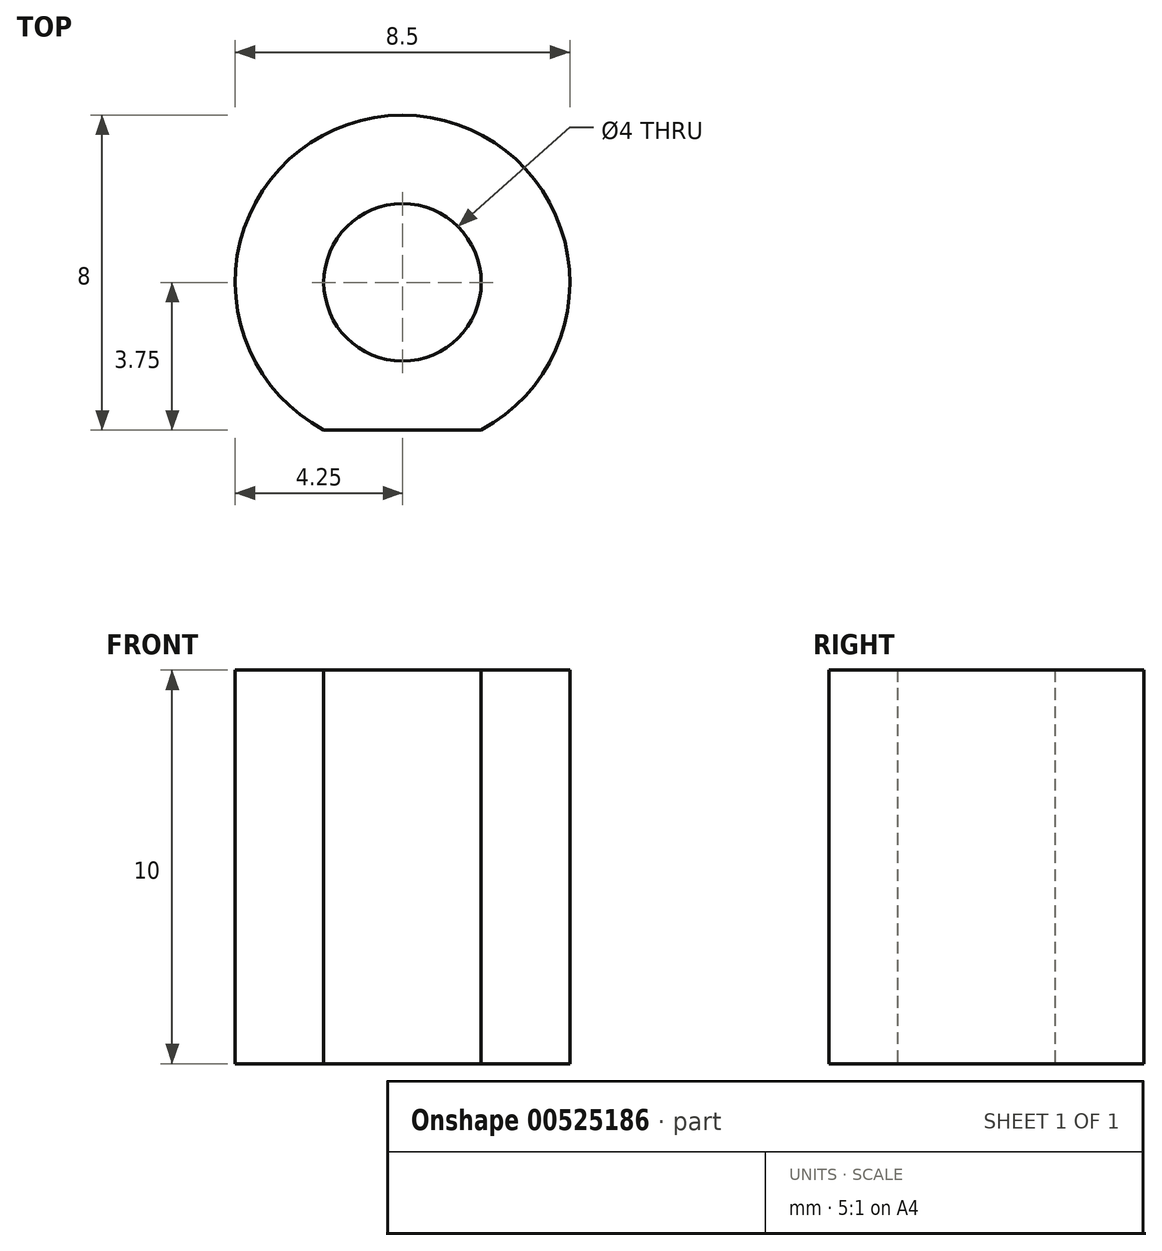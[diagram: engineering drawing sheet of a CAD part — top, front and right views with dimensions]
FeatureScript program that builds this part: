
annotation { "Feature Type Name" : "Feature", "Feature Type Description" : "" }
export const myFeature = defineFeature(function(context is Context, id is Id, definition is map)
    precondition{}
    {
        {
            var Q0;
            Q0=qCreatedBy(makeId("Top.planeOp"),FACE);
            var sketch = newSketch(context, id + "F0", { "sketchPlane" : qUnion([Q0])});
            skArc(sketch, "E0", {"start": v(2, -3.75) * mm, "mid": v(0, 4.25) * mm, "end": v(-2, -3.75) * mm});
            skLineSegment(sketch, "E1.bottom", {"start": v(-2, -3.75) * mm, "end": v(2, -3.75) * mm, "construction": true});
            skLineSegment(sketch, "E1.top", {"start": v(-2, 3.75) * mm, "end": v(2, 3.75) * mm, "construction": true});
            skLineSegment(sketch, "E1.left", {"start": v(-2, -3.75) * mm, "end": v(-2, 3.75) * mm, "construction": true});
            skLineSegment(sketch, "E1.right", {"start": v(2, -3.75) * mm, "end": v(2, 3.75) * mm, "construction": true});
            skLineSegment(sketch, "E2", {"start": v(-2, -3.75) * mm, "end": v(2, -3.75) * mm});
            skCircle(sketch, "E3", {"center": v(0, 0) * mm, "radius": 2 * mm});
            skSolve(sketch);
        }
        {
            var Q0;
            Q0 = qSketchRegion(id + "F0", true);
            extrude(context, id + "F1", {"entities" : qUnion([Q0]), "depth" : 10 * mm, "offsetDistance" : 25 * mm});
        }
    });
